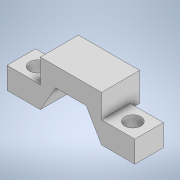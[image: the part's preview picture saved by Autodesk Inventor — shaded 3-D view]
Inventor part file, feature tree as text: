
AUTODESK INVENTOR PART (.ipt)
format: ipt  version: 2020.2 (Build 242310000, 310)  size: 145,920 bytes
history: native  units: mm
features: sketch x3, extrude x2, hole x1
ambient origin geometry x8: Origin, YZ Plane, XZ Plane, XY Plane, X Axis, Y Axis, Z Axis, Center Point
bodies: Solid1 (feature_tree)
feature tree (6):
  extrude  "Extrusion1"  Depth=6.4135mm
  extrude  "Extrusion2"  Depth=6.4262mm
  hole  "Hole2"  [1 undecoded]
  sketch  "Sketch1"  dims[d0=6.4135mm d1=6.4262mm]
  sketch  "Sketch3"  dims[d2=60.0deg d3=6.4262mm]
  sketch  "Sketch4"  dims[d4=120.0deg d5=6.4262mm d6=120.0deg d7=6.4262mm d8=120.0deg d9=6.4262mm d10=120.0deg d11=7.0mm d12=180.0deg d13=4.0mm d15=5.0mm d16=7.0mm d17=7.0mm d18=6.0mm d19=0.0mm d20=7.0mm d30=6.0mm d31=2.0mm d32=0.0mm d36=10.0mm d37=20.0mm d38=0.0mm d39=3.4mm d40=6.0mm d41=6.3mm d42=5.0mm d43=90.0deg d44=8.0mm d45=20.594885mm]
note: 1 required parameter value undecoded (feature->parameter linkage not recoverable at this tier; creation-order binding heuristic only, values carry confidence <= 0.55)
